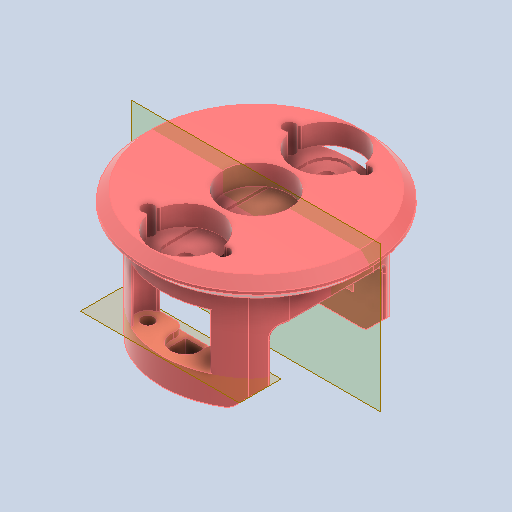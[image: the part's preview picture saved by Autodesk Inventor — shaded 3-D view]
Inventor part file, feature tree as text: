
AUTODESK INVENTOR PART (.ipt)
format: ipt  version: 2022 (Build 260153000, 153)  size: 466,944 bytes
history: native  units: in
note: dims shown in document units (in); Inventor stores cm internally (conversion verified against a paired STEP export)
features: sketch x13, other x3
ambient origin geometry x8: Origin, YZ Plane, XZ Plane, XY Plane, X Axis, Y Axis, Z Axis, Center Point
bodies: Solid1 (feature_tree)
feature tree (16):
  other  "Undercarriage.ipt"
  other  "Solid1::Undercarriage.ipt"
  other  "TaggingFeature1"
  sketch  "Sketch1"  dims[d0=0.3937in]
  sketch  "Sketch2"
  sketch  "Sketch9"
  sketch  "Sketch6"
  sketch  "Sketch7"
  sketch  "Sketch8"
  sketch  "Sketch10"
  sketch  "Sketch11"
  sketch  "Sketch12"
  sketch  "Sketch13"
  sketch  "Sketch14"
  sketch  "Sketch15"
  sketch  "Sketch16"
